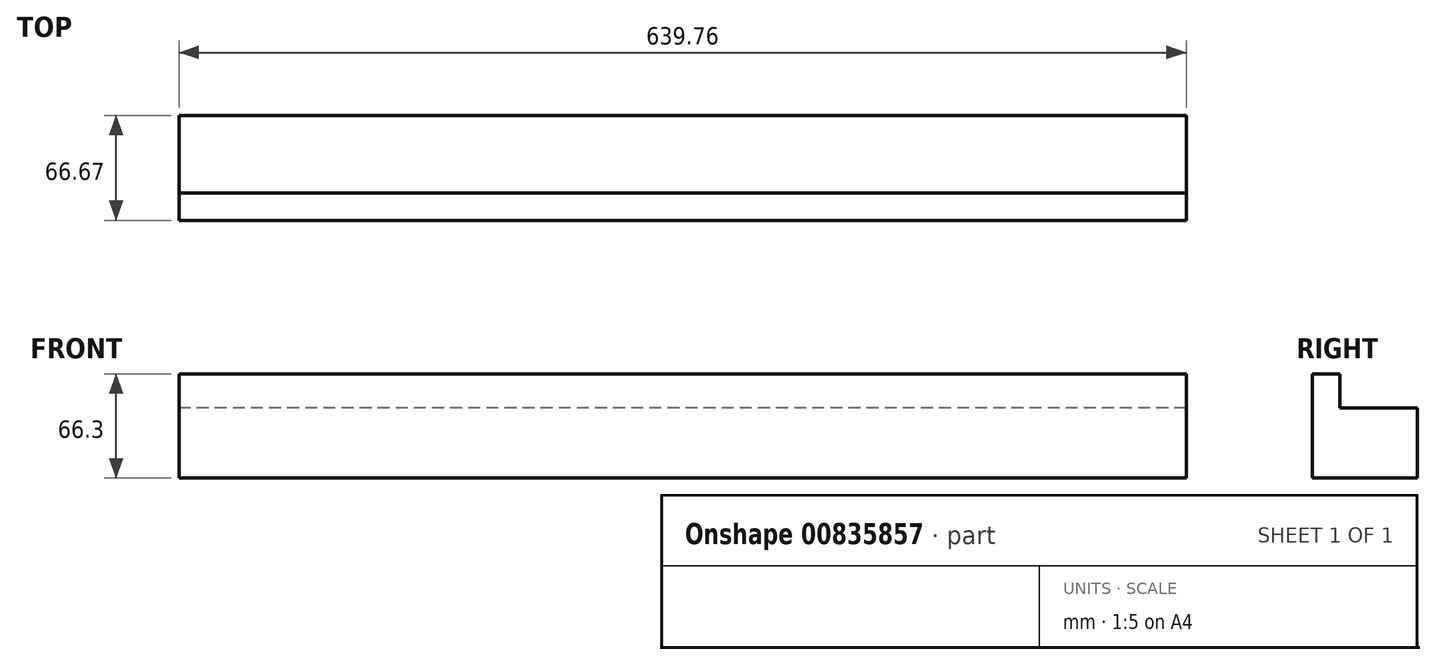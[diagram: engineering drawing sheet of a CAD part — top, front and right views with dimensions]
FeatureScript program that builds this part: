
annotation { "Feature Type Name" : "Feature", "Feature Type Description" : "" }
export const myFeature = defineFeature(function(context is Context, id is Id, definition is map)
    precondition{}
    {
        {
            var Q0;
            Q0=qCreatedBy(makeId("Right.planeOp"),FACE);
            var sketch = newSketch(context, id + "F0", { "sketchPlane" : qUnion([Q0])});
            skLineSegment(sketch, "E0", {"start": v(0, 23.03) * mm, "end": v(17.46, 23.03) * mm});
            skLineSegment(sketch, "E1", {"start": v(17.46, 23.03) * mm, "end": v(17.46, 1.18) * mm});
            skLineSegment(sketch, "E2", {"start": v(17.46, 1.18) * mm, "end": v(66.68, 1.18) * mm});
            skLineSegment(sketch, "E3", {"start": v(66.68, 1.18) * mm, "end": v(66.68, -43.27) * mm});
            skLineSegment(sketch, "E4", {"start": v(66.68, -43.27) * mm, "end": v(0, -43.27) * mm});
            skLineSegment(sketch, "E5", {"start": v(0, -43.27) * mm, "end": v(0, 23.03) * mm});
            skSolve(sketch);
        }
        {
            var Q0;
            Q0=makeQuery(id+"F0.imprint","IMPRINT",FACE,{"disambiguationData":[TD([[makeQuery(id+"F0.imprint","IMPRINT",EDGE,{"derivedFrom":sQuery(id+"F0.wireOp",EDGE,"E0")}),-1.0]])]});
            extrude(context, id + "F1", {"entities" : qUnion([Q0]), "depth" : 639.76 * mm, "offsetDistance" : 25.4 * mm});
        }
    });
